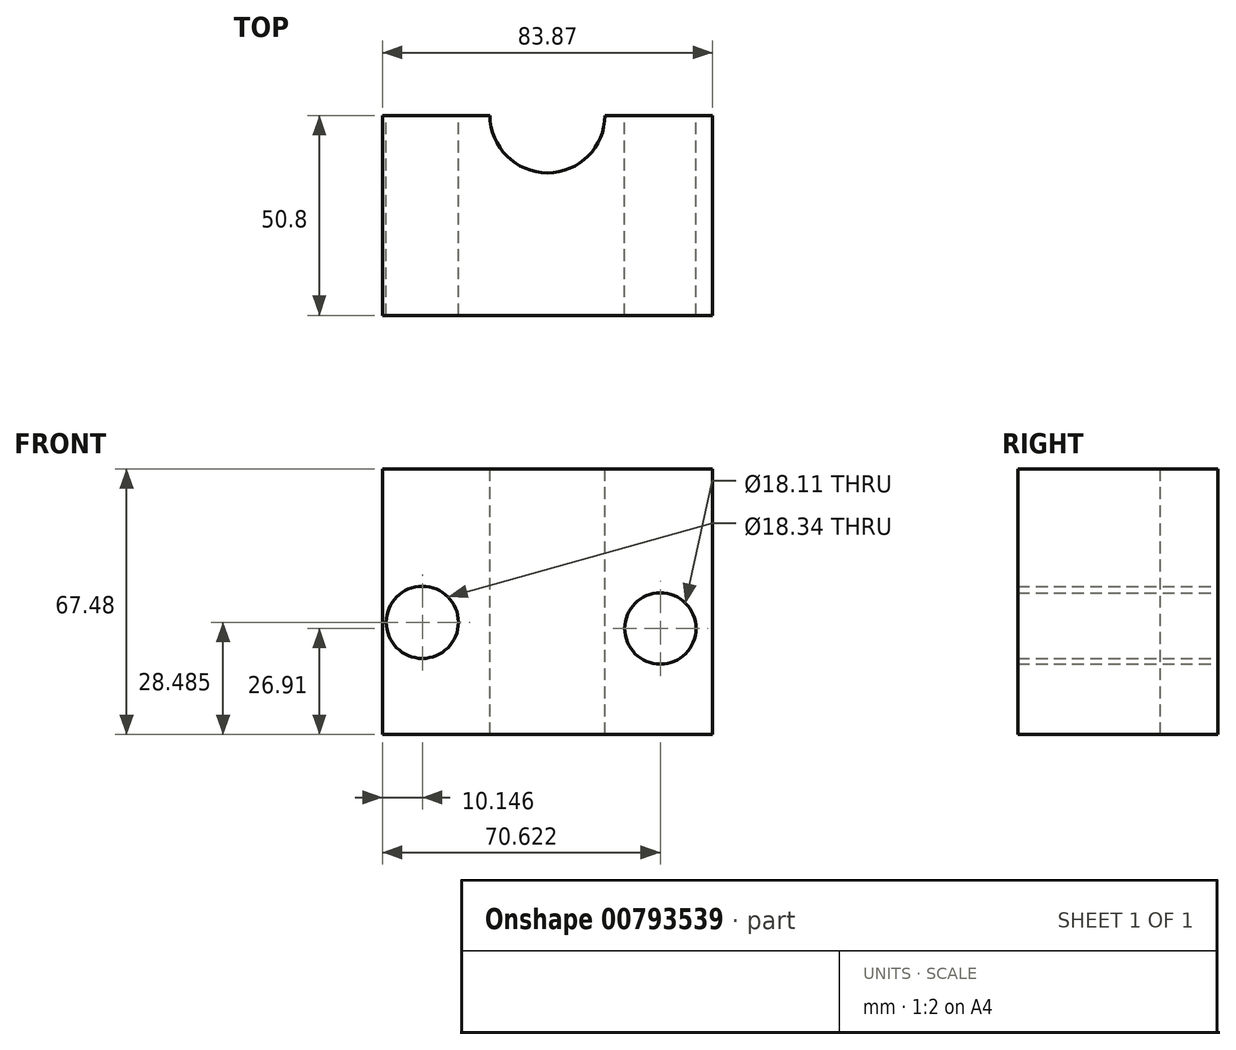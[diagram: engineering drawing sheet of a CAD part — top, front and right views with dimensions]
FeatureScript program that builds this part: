
annotation { "Feature Type Name" : "Feature", "Feature Type Description" : "" }
export const myFeature = defineFeature(function(context is Context, id is Id, definition is map)
    precondition{}
    {
        {
            var Q0;
            Q0=qCreatedBy(makeId("Front.planeOp"),FACE);
            var sketch = newSketch(context, id + "F0", { "sketchPlane" : qUnion([Q0])});
            skLineSegment(sketch, "E0.bottom", {"start": v(-36.27, 15.3) * mm, "end": v(47.6, 15.3) * mm});
            skLineSegment(sketch, "E0.top", {"start": v(-36.27, -52.18) * mm, "end": v(47.6, -52.18) * mm});
            skLineSegment(sketch, "E0.left", {"start": v(-36.27, 15.3) * mm, "end": v(-36.27, -52.18) * mm});
            skLineSegment(sketch, "E0.right", {"start": v(47.6, 15.3) * mm, "end": v(47.6, -52.18) * mm});
            skSolve(sketch);
        }
        {
            var Q0;
            Q0=makeQuery(id+"F0.imprint","IMPRINT",FACE,{"disambiguationData":[TD([[makeQuery(id+"F0.imprint","IMPRINT",EDGE,{"derivedFrom":sQuery(id+"F0.wireOp",EDGE,"E0.bottom")}),-1.0]])]});
            extrude(context, id + "F1", {"entities" : qUnion([Q0]), "depth" : 50.8 * mm, "offsetDistance" : 25.4 * mm});
        }
        {
            var Q0;
            Q0=makeQuery(id+"F1.opExtrude","SWEPT_FACE",FACE,{"disambiguationData":[OSD([sQuery(id+"F0.wireOp",EDGE,"E0.bottom")])]});
            var sketch = newSketch(context, id + "F2", { "sketchPlane" : qUnion([Q0])});
            skCircle(sketch, "E1", {"center": v(5.66, 0) * mm, "radius": 14.6 * mm});
            skSolve(sketch);
        }
        {
            var Q0;
            {var subQ0=sQuery(id+"F2.wireOp",EDGE,"E1");var subQ1=makeQuery(id+"F1.opExtrude","CAP_EDGE",EDGE,{"disambiguationData":[OSD([sQuery(id+"F0.wireOp",EDGE,"E0.bottom")])],"isStart":true});var subQ2=makeQuery(id+"F2.imprint","INTERSECT",VERTEX,{"disambiguationData":[OD(0.0)],"derivedFrom":[subQ1,subQ0]});Q0=makeQuery(id+"F2.imprint","IMPRINT",FACE,{"disambiguationData":[TD([[makeQuery(id+"F2.imprint","IMPRINT",EDGE,{"disambiguationData":[TD([[subQ2,-1.0]])],"derivedFrom":subQ0}),1.0]])]});}
            extrude(context, id + "F3", {"entities" : qUnion([Q0]), "operationType" : NewBodyOperationType.REMOVE, "oppositeDirection" : true, "depth" : 74.42 * mm, "offsetDistance" : 25.4 * mm});
        }
        {
            var Q0;
            {var subQ0=sQuery(id+"F0.wireOp",EDGE,"E0.bottom");var subQ1=sQuery(id+"F0.wireOp",EDGE,"E0.right");var subQ2=sQuery(id+"F0.wireOp",EDGE,"E0.top");Q0=makeQuery(id+"F3.boolean.opBoolean","SPLIT",FACE,{"disambiguationData":[TD([makeQuery(id+"F1.opExtrude","SWEPT_FACE",FACE,{"disambiguationData":[OSD([subQ1])]})])],"derivedFrom":makeQuery(id+"F1.opExtrude","CAP_FACE",FACE,{"disambiguationData":[OSD([subQ0,subQ2,sQuery(id+"F0.wireOp",EDGE,"E0.left"),subQ1])],"isStart":true})});}
            var sketch = newSketch(context, id + "F4", { "sketchPlane" : qUnion([Q0])});
            skCircle(sketch, "E2", {"center": v(-34.35, -25.27) * mm, "radius": 9.06 * mm});
            skCircle(sketch, "E3", {"center": v(26.12, -23.7) * mm, "radius": 9.17 * mm});
            skSolve(sketch);
        }
        {
            var Q0;
            Q0=makeQuery(id+"F4.imprint","IMPRINT",FACE,{"disambiguationData":[TD([[makeQuery(id+"F4.imprint","IMPRINT",EDGE,{"derivedFrom":sQuery(id+"F4.wireOp",EDGE,"E3")}),1.0]])]});
            var Q1;
            Q1=makeQuery(id+"F4.imprint","IMPRINT",FACE,{"disambiguationData":[TD([[makeQuery(id+"F4.imprint","IMPRINT",EDGE,{"derivedFrom":sQuery(id+"F4.wireOp",EDGE,"E2")}),1.0]])]});
            extrude(context, id + "F5", {"entities" : qUnion([Q0, Q1]), "operationType" : NewBodyOperationType.REMOVE, "oppositeDirection" : true, "depth" : 65.28 * mm, "offsetDistance" : 25.4 * mm});
        }
    });
